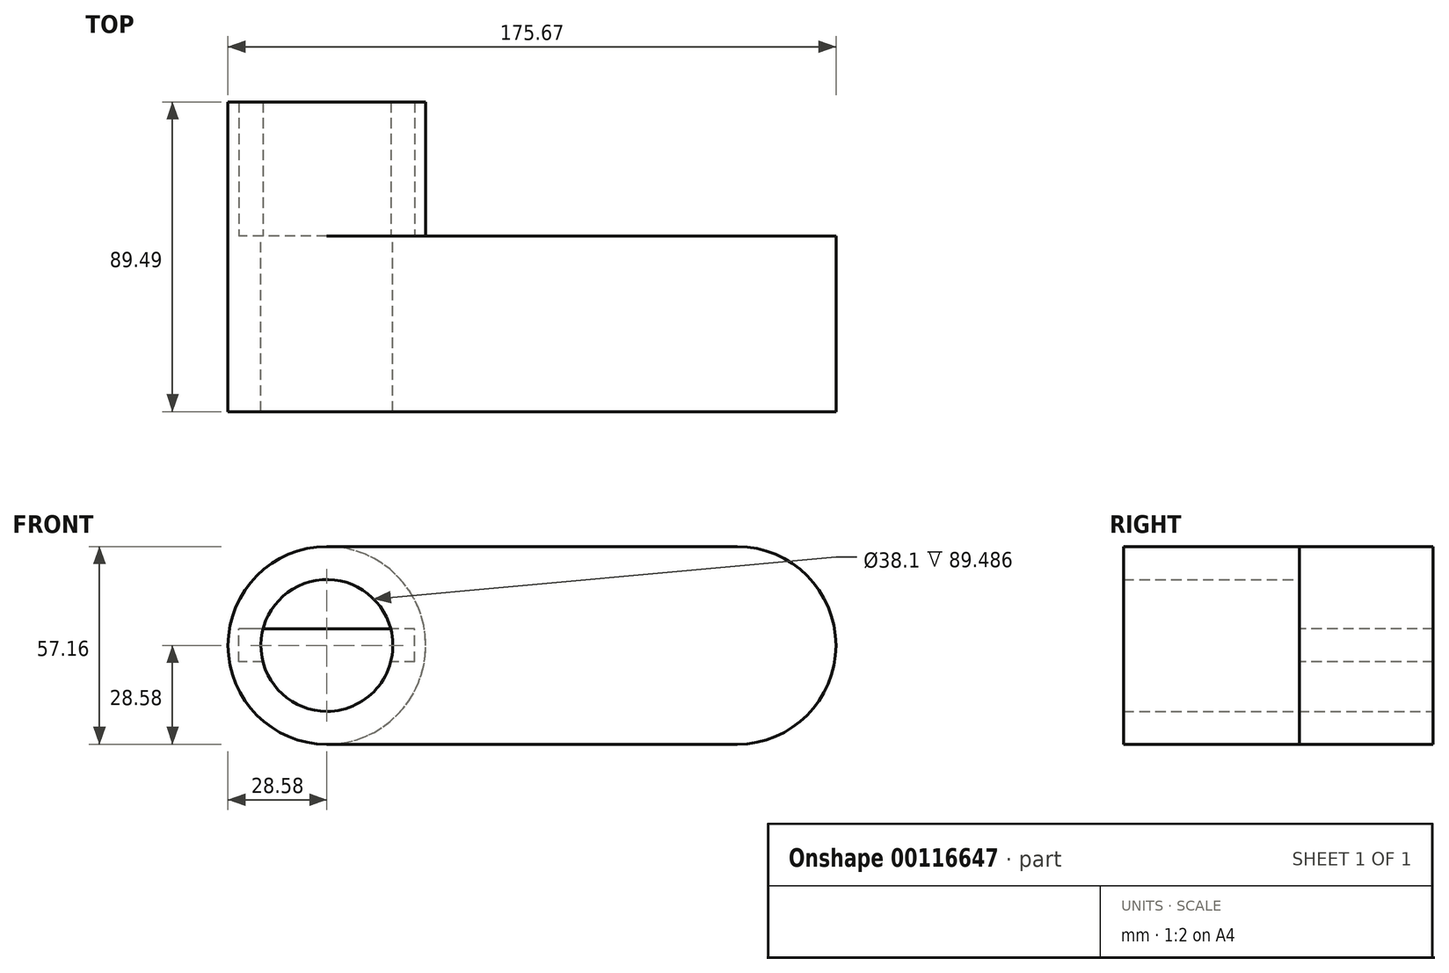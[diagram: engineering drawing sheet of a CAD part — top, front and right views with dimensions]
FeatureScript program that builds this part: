
annotation { "Feature Type Name" : "Feature", "Feature Type Description" : "" }
export const myFeature = defineFeature(function(context is Context, id is Id, definition is map)
    precondition{}
    {
        {
            var Q0;
            Q0=qCreatedBy(makeId("Front.planeOp"),FACE);
            var sketch = newSketch(context, id + "F0", { "sketchPlane" : qUnion([Q0])});
            skCircle(sketch, "E0", {"center": v(0, 0) * mm, "radius": 28.58 * mm});
            skCircle(sketch, "E1", {"center": v(118.51, 0) * mm, "radius": 28.57 * mm});
            skLineSegment(sketch, "E2", {"start": v(0, 28.58) * mm, "end": v(118.51, 28.58) * mm});
            skLineSegment(sketch, "E3", {"start": v(0, -28.58) * mm, "end": v(118.51, -28.57) * mm});
            skCircle(sketch, "E4", {"center": v(0, 0) * mm, "radius": 19.05 * mm});
            skCircle(sketch, "E5", {"center": v(118.51, 0) * mm, "radius": 19.05 * mm});
            skLineSegment(sketch, "E6.bottom", {"start": v(25.4, -4.76) * mm, "end": v(-25.4, -4.76) * mm});
            skLineSegment(sketch, "E6.top", {"start": v(25.4, 4.76) * mm, "end": v(-25.4, 4.76) * mm});
            skLineSegment(sketch, "E6.left", {"start": v(25.4, -4.76) * mm, "end": v(25.4, 4.76) * mm});
            skLineSegment(sketch, "E6.right", {"start": v(-25.4, -4.76) * mm, "end": v(-25.4, 4.76) * mm});
            skSolve(sketch);
        }
        {
            var Q0;
            {var subQ5=sQuery(id+"F0.wireOp",EDGE,"E6.right");Q0=makeQuery(id+"F0.imprint","IMPRINT",FACE,{"disambiguationData":[TD([[makeQuery(id+"F0.imprint","IMPRINT",EDGE,{"derivedFrom":subQ5}),-1.0]])]});}
            var Q1;
            Q1=makeQuery(id+"F0.imprint","IMPRINT",FACE,{"disambiguationData":[TD([[makeQuery(id+"F0.imprint","IMPRINT",EDGE,{"derivedFrom":sQuery(id+"F0.wireOp",EDGE,"E5")}),-1.0]])]});
            var Q2;
            {var subQ11=sQuery(id+"F0.wireOp",EDGE,"E6.left");Q2=makeQuery(id+"F0.imprint","IMPRINT",FACE,{"disambiguationData":[TD([[makeQuery(id+"F0.imprint","IMPRINT",EDGE,{"derivedFrom":subQ11}),-1.0]])]});}
            var Q3;
            {var subQ0=sQuery(id+"F0.wireOp",EDGE,"E2");Q3=makeQuery(id+"F0.imprint","IMPRINT",FACE,{"disambiguationData":[TD([[makeQuery(id+"F0.imprint","IMPRINT",EDGE,{"derivedFrom":subQ0}),-1.0]])]});}
            var Q4;
            Q4=makeQuery(id+"F0.imprint","IMPRINT",FACE,{"disambiguationData":[TD([[makeQuery(id+"F0.imprint","IMPRINT",EDGE,{"derivedFrom":sQuery(id+"F0.wireOp",EDGE,"E5")}),1.0]])]});
            var Q5;
            {var subQ5=sQuery(id+"F0.wireOp",EDGE,"E6.left");Q5=makeQuery(id+"F0.imprint","IMPRINT",FACE,{"disambiguationData":[TD([[makeQuery(id+"F0.imprint","IMPRINT",EDGE,{"derivedFrom":subQ5}),1.0]])]});}
            extrude(context, id + "F1", {"entities" : qUnion([Q0, Q1, Q2, Q3, Q4, Q5]), "depth" : 50.8 * mm});
        }
        {
            var Q0;
            {var subQ0=sQuery(id+"F0.wireOp",EDGE,"E6.top");var subQ1=sQuery(id+"F0.wireOp",EDGE,"E4");var subQ2=makeQuery(id+"F0.imprint","INTERSECT",VERTEX,{"disambiguationData":[OD(0.0)],"derivedFrom":[subQ1,subQ0]});Q0=makeQuery(id+"F0.imprint","IMPRINT",FACE,{"disambiguationData":[TD([[makeQuery(id+"F0.imprint","IMPRINT",EDGE,{"disambiguationData":[TD([[subQ2,-1.0]])],"derivedFrom":subQ1}),1.0]])]});}
            var Q1;
            {var subQ11=sQuery(id+"F0.wireOp",EDGE,"E6.left");Q1=makeQuery(id+"F0.imprint","IMPRINT",FACE,{"disambiguationData":[TD([[makeQuery(id+"F0.imprint","IMPRINT",EDGE,{"derivedFrom":subQ11}),-1.0]])]});}
            extrude(context, id + "F2", {"entities" : qUnion([Q0, Q1]), "operationType" : NewBodyOperationType.ADD, "oppositeDirection" : true, "depth" : 38.69 * mm});
        }
    });
